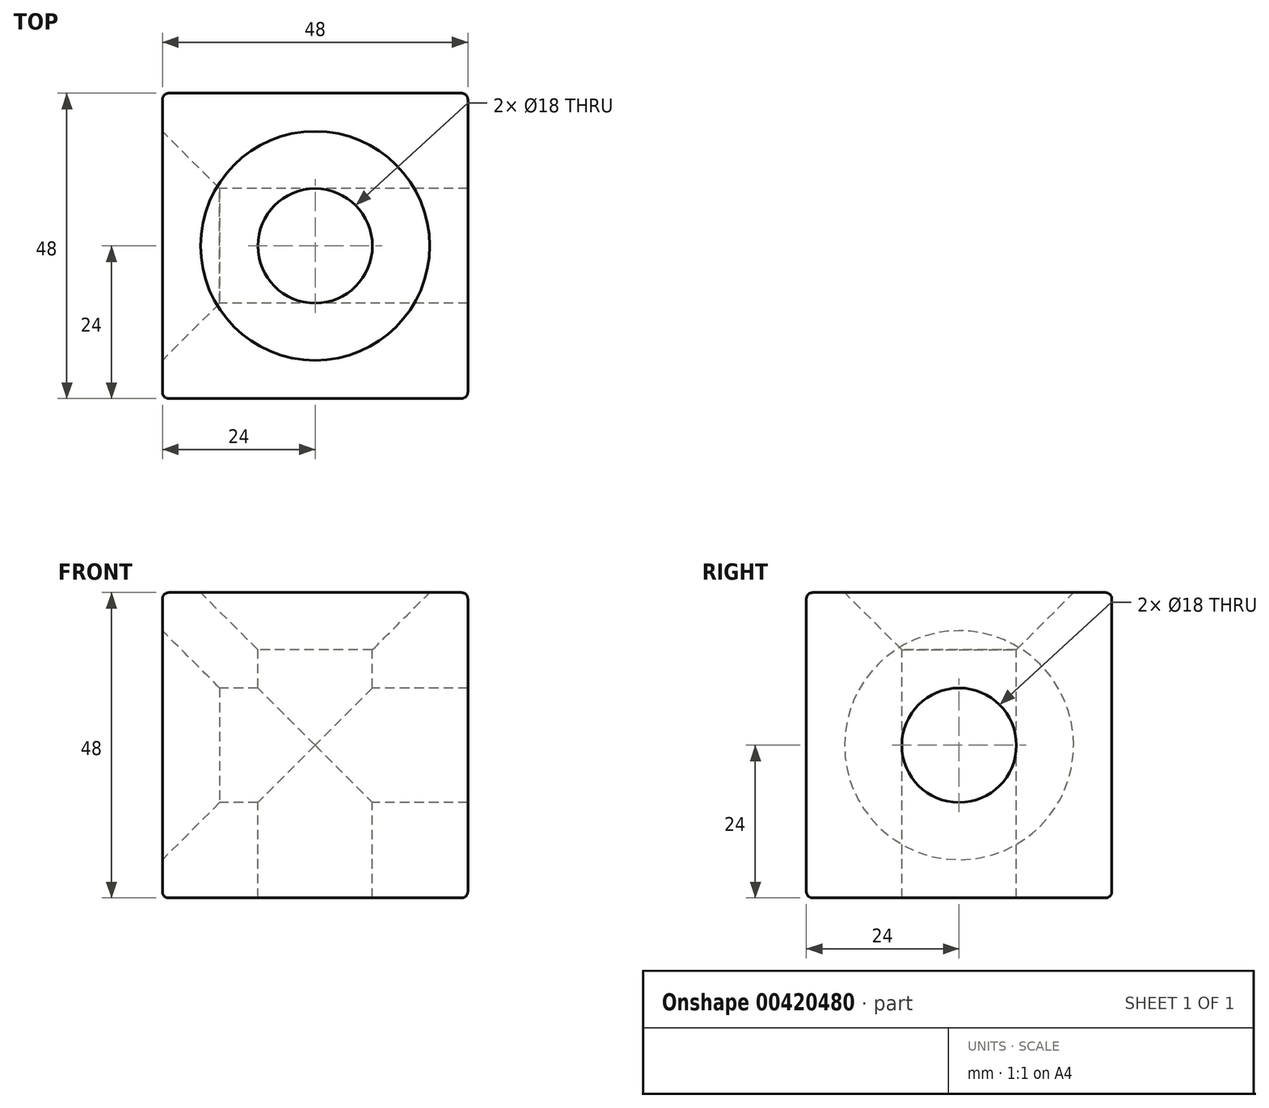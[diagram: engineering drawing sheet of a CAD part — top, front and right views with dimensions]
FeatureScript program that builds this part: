
annotation { "Feature Type Name" : "Feature", "Feature Type Description" : "" }
export const myFeature = defineFeature(function(context is Context, id is Id, definition is map)
    precondition{}
    {
        {
            var Q0;
            Q0=qCreatedBy(makeId("Front.planeOp"),FACE);
            var sketch = newSketch(context, id + "F0", { "sketchPlane" : qUnion([Q0])});
            skLineSegment(sketch, "E0.bottom", {"start": v(-24, 24) * mm, "end": v(24, 24) * mm});
            skLineSegment(sketch, "E0.top", {"start": v(-24, -24) * mm, "end": v(24, -24) * mm});
            skLineSegment(sketch, "E0.left", {"start": v(-24, 24) * mm, "end": v(-24, -24) * mm});
            skLineSegment(sketch, "E0.right", {"start": v(24, 24) * mm, "end": v(24, -24) * mm});
            skPoint(sketch, "E0.middle", {"position": v(0, 0) * mm});
            skSolve(sketch);
        }
        {
            var Q0;
            Q0=makeQuery(id+"F0.imprint","IMPRINT",FACE,{"disambiguationData":[TD([[makeQuery(id+"F0.imprint","IMPRINT",EDGE,{"derivedFrom":sQuery(id+"F0.wireOp",EDGE,"E0.bottom")}),-1.0]])]});
            extrude(context, id + "F1", {"entities" : qUnion([Q0]), "depth" : 48 * mm});
        }
        {
            var Q0;
            Q0=makeQuery(id+"F1.opExtrude","SWEPT_EDGE",EDGE,{"disambiguationData":[OSD([sQuery(id+"F0.wireOp",EDGE,"E0.bottom"),sQuery(id+"F0.wireOp",EDGE,"E0.right")])]});
            fillet(context, id + "F2", {"entities" : qUnion([Q0]), "radius" : 1 * mm, "tangentPropagation" : true, "allowEdgeOverflow" : false});
        }
        {
            var Q0;
            Q0=makeQuery(id+"F1.opExtrude","SWEPT_EDGE",EDGE,{"disambiguationData":[OSD([sQuery(id+"F0.wireOp",EDGE,"E0.bottom"),sQuery(id+"F0.wireOp",EDGE,"E0.left")])]});
            var Q1;
            Q1=makeQuery(id+"F1.opExtrude","CAP_EDGE",EDGE,{"disambiguationData":[OSD([sQuery(id+"F0.wireOp",EDGE,"E0.bottom")])],"isStart":true});
            var Q2;
            Q2=makeQuery(id+"F1.opExtrude","CAP_EDGE",EDGE,{"disambiguationData":[OSD([sQuery(id+"F0.wireOp",EDGE,"E0.bottom")])],"isStart":false});
            fillet(context, id + "F3", {"entities" : qUnion([Q0, Q1, Q2]), "radius" : 1 * mm, "tangentPropagation" : true, "allowEdgeOverflow" : false});
        }
        {
            var Q0;
            Q0=makeQuery(id+"F1.opExtrude","CAP_EDGE",EDGE,{"disambiguationData":[OSD([sQuery(id+"F0.wireOp",EDGE,"E0.left")])],"isStart":false});
            var Q1;
            {var subQ0=sQuery(id+"F0.wireOp",EDGE,"E0.right");Q1=makeQuery(id+"F3.opFillet","BLEND_EDGE",EDGE,{"blendedFrom":[makeQuery(id+"F1.opExtrude","CAP_EDGE",EDGE,{"disambiguationData":[OSD([subQ0])],"isStart":false}),makeQuery(id+"F1.opExtrude","CAP_FACE",FACE,{"disambiguationData":[OSD([sQuery(id+"F0.wireOp",EDGE,"E0.bottom"),sQuery(id+"F0.wireOp",EDGE,"E0.top"),sQuery(id+"F0.wireOp",EDGE,"E0.left"),subQ0])],"isStart":false})],"blendedInto":[makeQuery(id+"F1.opExtrude","CAP_FACE",FACE,{"disambiguationData":[OSD([sQuery(id+"F0.wireOp",EDGE,"E0.bottom"),sQuery(id+"F0.wireOp",EDGE,"E0.top"),sQuery(id+"F0.wireOp",EDGE,"E0.left"),subQ0])],"isStart":false})]});}
            var Q2;
            {var subQ0=sQuery(id+"F0.wireOp",EDGE,"E0.right");Q2=makeQuery(id+"F3.opFillet","BLEND_EDGE",EDGE,{"blendedFrom":[makeQuery(id+"F1.opExtrude","CAP_EDGE",EDGE,{"disambiguationData":[OSD([subQ0])],"isStart":true}),makeQuery(id+"F1.opExtrude","CAP_FACE",FACE,{"disambiguationData":[OSD([sQuery(id+"F0.wireOp",EDGE,"E0.bottom"),sQuery(id+"F0.wireOp",EDGE,"E0.top"),sQuery(id+"F0.wireOp",EDGE,"E0.left"),subQ0])],"isStart":true})],"blendedInto":[makeQuery(id+"F1.opExtrude","CAP_FACE",FACE,{"disambiguationData":[OSD([sQuery(id+"F0.wireOp",EDGE,"E0.bottom"),sQuery(id+"F0.wireOp",EDGE,"E0.top"),sQuery(id+"F0.wireOp",EDGE,"E0.left"),subQ0])],"isStart":true})]});}
            var Q3;
            Q3=makeQuery(id+"F1.opExtrude","CAP_EDGE",EDGE,{"disambiguationData":[OSD([sQuery(id+"F0.wireOp",EDGE,"E0.left")])],"isStart":true});
            var Q4;
            Q4=makeQuery(id+"F1.opExtrude","CAP_EDGE",EDGE,{"disambiguationData":[OSD([sQuery(id+"F0.wireOp",EDGE,"E0.top")])],"isStart":true});
            var Q5;
            Q5=makeQuery(id+"F1.opExtrude","SWEPT_EDGE",EDGE,{"disambiguationData":[OSD([sQuery(id+"F0.wireOp",EDGE,"E0.top"),sQuery(id+"F0.wireOp",EDGE,"E0.left")])]});
            var Q6;
            Q6=makeQuery(id+"F1.opExtrude","CAP_EDGE",EDGE,{"disambiguationData":[OSD([sQuery(id+"F0.wireOp",EDGE,"E0.top")])],"isStart":false});
            var Q7;
            Q7=makeQuery(id+"F1.opExtrude","SWEPT_EDGE",EDGE,{"disambiguationData":[OSD([sQuery(id+"F0.wireOp",EDGE,"E0.top"),sQuery(id+"F0.wireOp",EDGE,"E0.right")])]});
            fillet(context, id + "F4", {"entities" : qUnion([Q0, Q1, Q2, Q3, Q4, Q5, Q6, Q7]), "radius" : 1 * mm, "tangentPropagation" : true, "allowEdgeOverflow" : false});
        }
        {
            var Q0;
            Q0=makeQuery(id+"F1.opExtrude","SWEPT_FACE",FACE,{"disambiguationData":[OSD([sQuery(id+"F0.wireOp",EDGE,"E0.bottom")])]});
            var sketch = newSketch(context, id + "F5", { "sketchPlane" : qUnion([Q0])});
            skPoint(sketch, "E1", {"position": v(0, -24) * mm});
            skPoint(sketch, "E1.positionSnap0", {"position": v(23, -24) * mm});
            skSolve(sketch);
        }
        {
            var Q0;
            Q0=sQuery(id+"F5.wireOp",VERTEX,"E1");
            var Q1;
            Q1=makeQuery(id+"F1.opExtrude","SWEPT_BODY",BODY,{"disambiguationData":[OSD([sQuery(id+"F0.wireOp",EDGE,"E0.bottom"),sQuery(id+"F0.wireOp",EDGE,"E0.top"),sQuery(id+"F0.wireOp",EDGE,"E0.left"),sQuery(id+"F0.wireOp",EDGE,"E0.right")])]});
            hole(context, id + "F6", {"style" : HoleStyle.C_SINK, "endStyle" : HoleEndStyle.THROUGH, "holeDiameter" : 18 * mm, "cSinkDiameter" : 36 * mm, "cSinkAngle" : 90 * degree, "isTappedThrough" : true, "tappedDepth" : 12 * mm, "tapClearance" : 3, "locations" : qUnion([Q0]), "scope" : qUnion([Q1])});
        }
        {
            var Q0;
            Q0=makeQuery(id+"F1.opExtrude","SWEPT_FACE",FACE,{"disambiguationData":[OSD([sQuery(id+"F0.wireOp",EDGE,"E0.left")])]});
            var sketch = newSketch(context, id + "F7", { "sketchPlane" : qUnion([Q0])});
            skPoint(sketch, "E2", {"position": v(24, 0) * mm});
            skPoint(sketch, "E2.positionSnap0", {"position": v(24, 23) * mm});
            skSolve(sketch);
        }
        {
            var Q0;
            Q0=sQuery(id+"F7.wireOp",VERTEX,"E2");
            var Q1;
            Q1=makeQuery(id+"F1.opExtrude","SWEPT_BODY",BODY,{"disambiguationData":[OSD([sQuery(id+"F0.wireOp",EDGE,"E0.bottom"),sQuery(id+"F0.wireOp",EDGE,"E0.top"),sQuery(id+"F0.wireOp",EDGE,"E0.left"),sQuery(id+"F0.wireOp",EDGE,"E0.right")])]});
            hole(context, id + "F8", {"style" : HoleStyle.C_SINK, "endStyle" : HoleEndStyle.THROUGH, "holeDiameter" : 18 * mm, "cSinkDiameter" : 36 * mm, "cSinkAngle" : 90 * degree, "isTappedThrough" : true, "tappedDepth" : 12 * mm, "tapClearance" : 3, "locations" : qUnion([Q0]), "scope" : qUnion([Q1])});
        }
    });
